# Revit family: Digital_Media-Honeywell-VARIODYN_D1-583361(2)-22
name_source: partatom
category: Electrical Equipment
revit_build: Autodesk Revit 2017 (Build: 20160225_1515(x64)
units: mm (PartAtom-declared; Revit-internal decimal feet)

## family parameters
Cut with Voids When Loaded = No
Host = Face
OmniClass Number = 23.85.50.00
OmniClass Title = Communication Systems
Part Type = Other Panel
Room Calculation Point = No
Round Connector Dimension = Use Diameter
Shared = No

## types (2) — shared parameters
Air Humidity = 15 ... 90 % (non-condensing)
Ambient Temperature = -5 °C ... 55 °C
Apparent Load = 0 VA
Default Elevation = 1219 mm
Finish = Metal - Honeywell - Stainless Steel - Black
Frequency = 47 Hz
Height = 44 mm  [stored 0.144357 ft]
Manufacturer = Honeywell International
Manufacturer Fax Number = 02131/40615-606
Number of Poles = 1
Power Consumption = 50 / 80 W
Power Factor = 1
Product Documentation Link = https://www.esser-systems.com
Product Page URL = https://www.esser-systems.com
Rated Frequency = 47 ... 63 Hz
Rated Voltage = 90 ... 254 V AC
URL = www.esser-systems.com
Utility = No
Version = 2017 - v1.0a
Voltage = 90
Watts = 50 W
Width = 483 mm

## per-type parameters (varying)
| type | Constraints | Depth | Description | Load Sub-Classification | Model | Product Name | Weight |
| DOM4-8 - 8 Loudspeakers - 583361 | 1 | 345 mm | Digital Output Module DOM4-8 | Yes | 583361.22 | DOM4-8 | 5.70 kgf |
| DOM4-24 - 24 Loudspeakers - 583362 | 2 | 349 mm  [stored 1.14501 ft] | Digital Output Module DOM4-24 | No | 583362.22 | DOM4-24 | 6.80 kgf |

note: [stored X ft] marks values corroborated as IEEE doubles in the binary element streams (Revit-internal decimal feet)

## geometry (parser evidence)
native form markers: Sweep x1
no freeform markers — native parametric forms only
